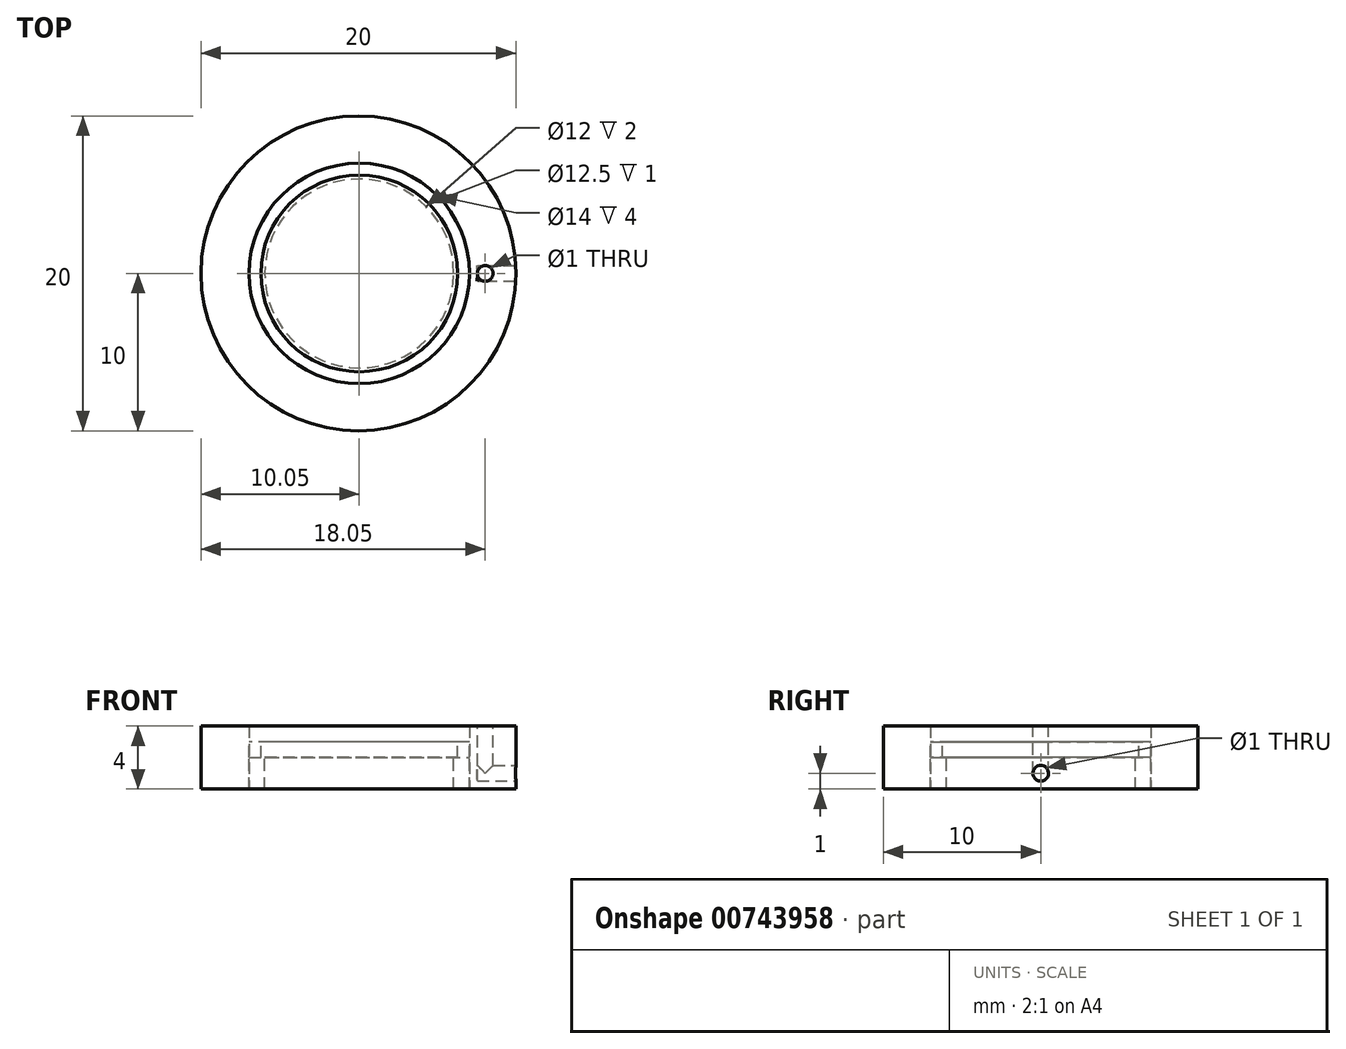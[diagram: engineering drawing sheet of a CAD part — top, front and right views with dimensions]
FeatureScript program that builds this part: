
annotation { "Feature Type Name" : "Feature", "Feature Type Description" : "" }
export const myFeature = defineFeature(function(context is Context, id is Id, definition is map)
    precondition{}
    {
        {
            var Q0;
            Q0=qCreatedBy(makeId("Top.planeOp"),FACE);
            var sketch = newSketch(context, id + "F0", { "sketchPlane" : qUnion([Q0])});
            skCircle(sketch, "E0", {"center": v(0, 0) * mm, "radius": 6.25 * mm});
            skSolve(sketch);
        }
        {
            var Q0;
            Q0=makeQuery(id+"F0.imprint","IMPRINT",FACE,{"disambiguationData":[TD([[makeQuery(id+"F0.imprint","IMPRINT",EDGE,{"derivedFrom":sQuery(id+"F0.wireOp",EDGE,"E0")}),1.0]])]});
            extrude(context, id + "F1", {"entities" : qUnion([Q0]), "depth" : 1 * mm, "offsetDistance" : 25 * mm});
        }
        {
            var Q0;
            Q0=makeQuery(id+"F1.opExtrude","CAP_FACE",FACE,{"disambiguationData":[OSD([sQuery(id+"F0.wireOp",EDGE,"E0")])],"isStart":false});
            var sketch = newSketch(context, id + "F2", { "sketchPlane" : qUnion([Q0])});
            skCircle(sketch, "E1", {"center": v(0, 0) * mm, "radius": 6.25 * mm});
            skCircle(sketch, "E2", {"center": v(0, 0) * mm, "radius": 7 * mm});
            skSolve(sketch);
        }
        {
            var Q0;
            Q0 = qSketchRegion(id + "F2", true);
            var Q1;
            Q1=makeQuery(id+"F1.opExtrude","CAP_FACE",FACE,{"disambiguationData":[OSD([sQuery(id+"F0.wireOp",EDGE,"E0")])],"isStart":true});
            extrude(context, id + "F3", {"entities" : qUnion([Q0]), "endBound" : BoundingType.UP_TO_SURFACE, "oppositeDirection" : true, "depth" : 25 * mm, "endBoundEntityFace" : qUnion([Q1]), "offsetDistance" : 25 * mm});
        }
        {
            var Q0;
            Q0=makeQuery(id+"F1.opExtrude","CAP_FACE",FACE,{"disambiguationData":[OSD([sQuery(id+"F0.wireOp",EDGE,"E0")])],"isStart":true});
            var sketch = newSketch(context, id + "F4", { "sketchPlane" : qUnion([Q0])});
            skCircle(sketch, "E3", {"center": v(0, 0) * mm, "radius": 7 * mm});
            skCircle(sketch, "E4", {"center": v(0, 0) * mm, "radius": 6 * mm});
            skSolve(sketch);
        }
        {
            var Q0;
            Q0 = qSketchRegion(id + "F4", true);
            extrude(context, id + "F5", {"entities" : qUnion([Q0]), "depth" : 2 * mm, "offsetDistance" : 25 * mm});
        }
        {
            var Q0;
            Q0=makeQuery(id+"F5.opExtrude","CAP_FACE",FACE,{"disambiguationData":[OSD([sQuery(id+"F4.wireOp",EDGE,"E3"),sQuery(id+"F4.wireOp",EDGE,"E4")])],"isStart":false});
            var sketch = newSketch(context, id + "F6", { "sketchPlane" : qUnion([Q0])});
            skCircle(sketch, "E5", {"center": v(0, 0) * mm, "radius": 7 * mm});
            skCircle(sketch, "E6", {"center": v(-0.05, 0) * mm, "radius": 10 * mm});
            skSolve(sketch);
        }
        {
            var Q0;
            Q0 = qSketchRegion(id + "F6", true);
            var Q1;
            Q1=makeQuery(id+"F1.opExtrude","CAP_FACE",FACE,{"disambiguationData":[OSD([sQuery(id+"F0.wireOp",EDGE,"E0")])],"isStart":false});
            extrude(context, id + "F7", {"entities" : qUnion([Q0]), "endBound" : BoundingType.UP_TO_SURFACE, "oppositeDirection" : true, "depth" : 25 * mm, "endBoundEntityFace" : qUnion([Q1]), "hasOffset" : true, "offsetDistance" : 1 * mm, "offsetOppositeDirection" : true});
        }
        {
            var Q0;
            Q0=qCreatedBy(makeId("Right.planeOp"),FACE);
            cPlane(context, id + "F8", {"entities" : qUnion([Q0]), "cplaneType" : CPlaneType.OFFSET, "offset" : 10 * mm, "width" : 150 * mm, "height" : 150 * mm});
        }
        {
            var Q0;
            Q0=qCreatedBy(id+"F8.planeOp",FACE);
            var sketch = newSketch(context, id + "F9", { "sketchPlane" : qUnion([Q0])});
            skPoint(sketch, "E7", {"position": v(0, -1) * mm});
            skCircle(sketch, "E8", {"center": v(0, -1) * mm, "radius": 0.5 * mm});
            skSolve(sketch);
        }
        {
            var Q0;
            Q0 = qSketchRegion(id + "F9", true);
            var Q1;
            Q1=makeQuery(id+"F5.opExtrude","SWEPT_FACE",FACE,{"disambiguationData":[OSD([sQuery(id+"F4.wireOp",EDGE,"E3")])]});
            extrude(context, id + "F10", {"entities" : qUnion([Q0]), "operationType" : NewBodyOperationType.REMOVE, "endBound" : BoundingType.UP_TO_SURFACE, "oppositeDirection" : true, "depth" : 25 * mm, "endBoundEntityFace" : qUnion([Q1]), "hasOffset" : true, "offsetDistance" : .5 * mm});
        }
        {
            var Q0;
            Q0=makeQuery(id+"F7.opExtrude","CAP_FACE",FACE,{"disambiguationData":[OSD([sQuery(id+"F6.wireOp",EDGE,"E5"),sQuery(id+"F6.wireOp",EDGE,"E6")])],"isStart":false});
            var sketch = newSketch(context, id + "F11", { "sketchPlane" : qUnion([Q0])});
            skPoint(sketch, "E9", {"position": v(8, 0) * mm});
            skCircle(sketch, "E10", {"center": v(8, 0) * mm, "radius": 0.5 * mm});
            skSolve(sketch);
        }
        {
            var Q0;
            Q0 = qSketchRegion(id + "F11", true);
            var Q1;
            Q1=makeQuery(id+"F10.boolean.opBoolean","COPY",FACE,{"derivedFrom":makeQuery(id+"F10.opExtrude","SWEPT_FACE",FACE,{"disambiguationData":[OSD([sQuery(id+"F9.wireOp",EDGE,"E8")])]})});
            extrude(context, id + "F12", {"entities" : qUnion([Q0]), "operationType" : NewBodyOperationType.REMOVE, "endBound" : BoundingType.UP_TO_NEXT, "oppositeDirection" : true, "depth" : 25 * mm, "endBoundEntityFace" : qUnion([Q1]), "offsetDistance" : 25 * mm});
        }
    });
